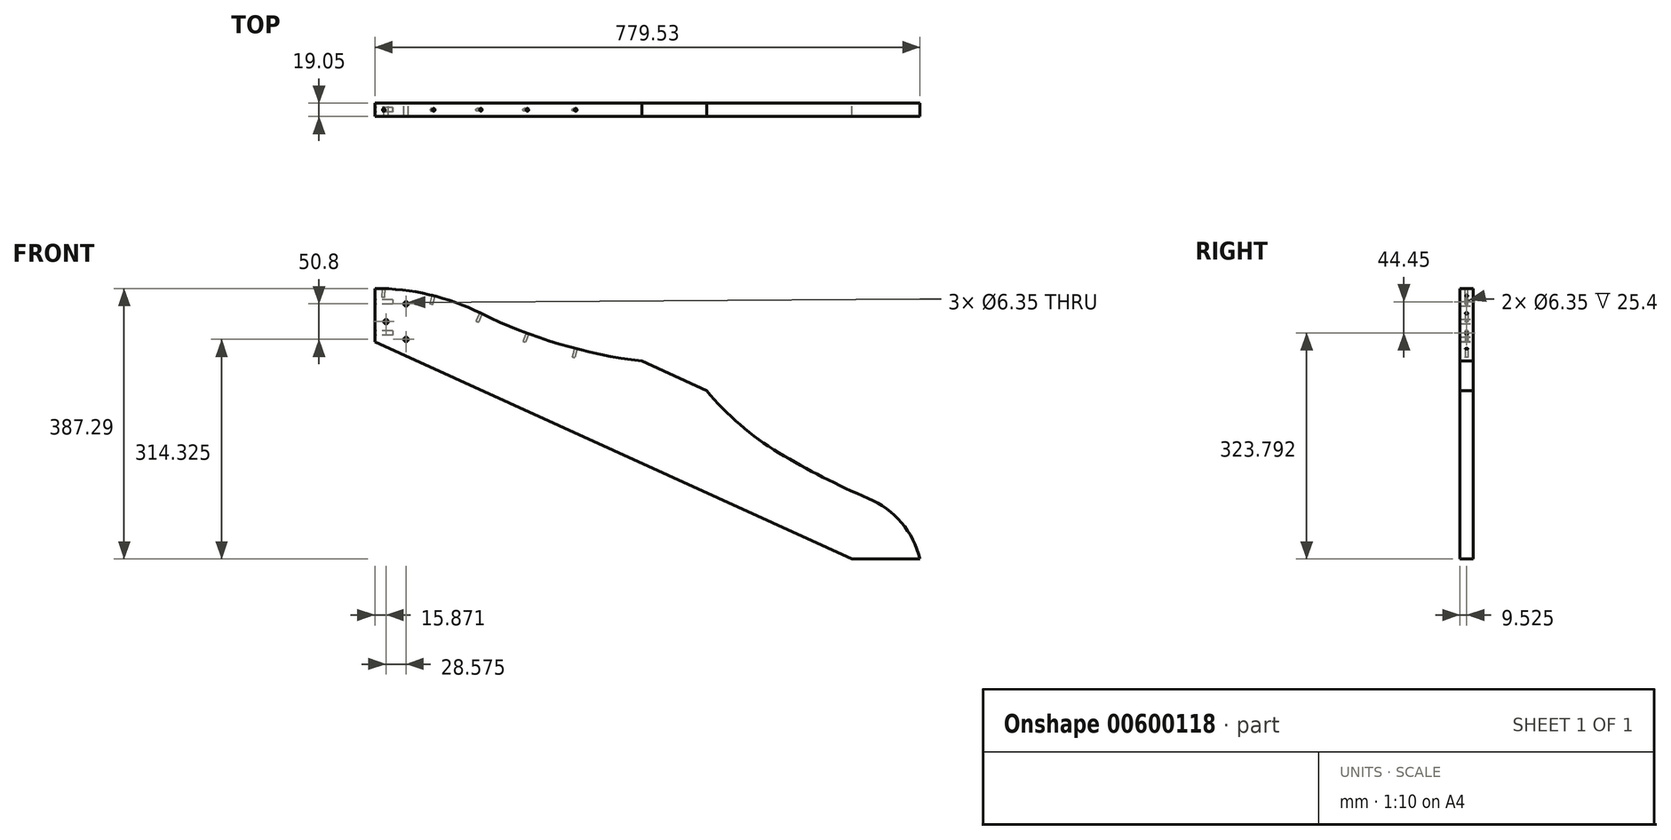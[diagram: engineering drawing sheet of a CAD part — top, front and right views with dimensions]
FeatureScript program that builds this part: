
annotation { "Feature Type Name" : "Feature", "Feature Type Description" : "" }
export const myFeature = defineFeature(function(context is Context, id is Id, definition is map)
    precondition{}
    {
        {
            var Q0;
            Q0=qCreatedBy(makeId("Front.planeOp"),FACE);
            var sketch = newSketch(context, id + "F0", { "sketchPlane" : qUnion([Q0])});
            skLineSegment(sketch, "E0", {"start": v(-749.3, 0) * mm, "end": v(-781.05, 69.67) * mm});
            skLineSegment(sketch, "E1", {"start": v(-390.53, 133.35) * mm, "end": v(-288.93, 133.35) * mm});
            skArc(sketch, "E2", {"start": v(-628.65, 100.15) * mm, "mid": v(-706.61, 93.72) * mm, "end": v(-781.05, 69.67) * mm});
            skArc(sketch, "E3", {"start": v(-628.65, 100.15) * mm, "mid": v(-508.16, 106.52) * mm, "end": v(-390.52, 133.35) * mm});
            skPoint(sketch, "E4", {"position": v(88.9, 40.51) * mm});
            skLineSegment(sketch, "E5", {"start": v(0, 0) * mm, "end": v(-749.3, 0) * mm});
            skLineSegment(sketch, "E6", {"start": v(0, 0) * mm, "end": v(88.9, 40.51) * mm});
            skArc(sketch, "E7", {"start": v(-288.93, 133.35) * mm, "mid": v(-225.13, 108.78) * mm, "end": v(-158.13, 95.25) * mm});
            skArc(sketch, "E8", {"start": v(-158.13, 95.25) * mm, "mid": v(-86.32, 89.52) * mm, "end": v(-14.28, 88.9) * mm});
            skArc(sketch, "E9", {"start": v(88.9, 40.51) * mm, "mid": v(43.04, 76.93) * mm, "end": v(-14.28, 88.9) * mm});
            skLineSegment(sketch, "E10", {"start": v(0, 0) * mm, "end": v(-620.44, -282.75) * mm, "construction": true});
            skLineSegment(sketch, "E11", {"start": v(-620.44, -282.75) * mm, "end": v(-749.3, 0) * mm, "construction": true});
            skLineSegment(sketch, "E12", {"start": v(-731.4, 67.93) * mm, "end": v(-710.34, 21.7) * mm, "construction": true});
            skLineSegment(sketch, "E13", {"start": v(-720.88, 44.82) * mm, "end": v(-746.88, 32.97) * mm, "construction": true});
            skCircle(sketch, "E14", {"center": v(-731.4, 67.93) * mm, "radius": 3.18 * mm});
            skCircle(sketch, "E15", {"center": v(-710.34, 21.7) * mm, "radius": 3.18 * mm});
            skCircle(sketch, "E16", {"center": v(-746.88, 32.97) * mm, "radius": 3.18 * mm});
            skLineSegment(sketch, "E17.bottom", {"start": v(-798.38, 61.77) * mm, "end": v(-781.05, 69.67) * mm, "construction": true});
            skLineSegment(sketch, "E17.top", {"start": v(-761.52, -19.13) * mm, "end": v(-744.18, -11.23) * mm, "construction": true});
            skLineSegment(sketch, "E17.left", {"start": v(-798.38, 61.77) * mm, "end": v(-761.52, -19.13) * mm, "construction": true});
            skLineSegment(sketch, "E17.right", {"start": v(-781.05, 69.67) * mm, "end": v(-744.18, -11.23) * mm, "construction": true});
            skLineSegment(sketch, "E18", {"start": v(0, 0) * mm, "end": v(97.7, 0) * mm, "construction": true});
            skLineSegment(sketch, "E19", {"start": v(97.7, 0) * mm, "end": v(88.9, 40.51) * mm, "construction": true});
            skLineSegment(sketch, "E20", {"start": v(-719.34, 102.7) * mm, "end": v(-674.51, 4.33) * mm, "construction": true});
            skSolve(sketch);
        }
        {
            var Q0;
            Q0=qCreatedBy(makeId("Front.planeOp"),FACE);
            var sketch = newSketch(context, id + "F1", { "sketchPlane" : qUnion([Q0])});
            skArc(sketch, "E21", {"start": v(-626.17, 175.74) * mm, "mid": v(-742.2, 163.18) * mm, "end": v(-850.18, 118.89) * mm, "construction": true});
            skArc(sketch, "E22", {"start": v(-626.17, 175.74) * mm, "mid": v(-492.66, 185.6) * mm, "end": v(-364.26, 223.48) * mm, "construction": true});
            skLineSegment(sketch, "E23", {"start": v(-605.52, 804.8) * mm, "end": v(-605.52, 101.3) * mm, "construction": true});
            skLineSegment(sketch, "E24", {"start": v(-805.94, 80.59) * mm, "end": v(-798.84, 62.9) * mm, "construction": true});
            skLineSegment(sketch, "E25", {"start": v(-798.84, 62.9) * mm, "end": v(-739.92, 86.57) * mm, "construction": true});
            skLineSegment(sketch, "E26", {"start": v(-739.92, 86.57) * mm, "end": v(-747.01, 104.25) * mm, "construction": true});
            skLineSegment(sketch, "E27", {"start": v(-747.01, 104.25) * mm, "end": v(-805.94, 80.59) * mm, "construction": true});
            skLineSegment(sketch, "E28", {"start": v(-731.46, 89.3) * mm, "end": v(-668.96, 100.57) * mm, "construction": true});
            skLineSegment(sketch, "E29", {"start": v(-668.96, 100.57) * mm, "end": v(-672.34, 119.31) * mm, "construction": true});
            skLineSegment(sketch, "E30", {"start": v(-672.34, 119.31) * mm, "end": v(-734.83, 108.05) * mm, "construction": true});
            skLineSegment(sketch, "E31", {"start": v(-734.83, 108.05) * mm, "end": v(-731.46, 89.3) * mm, "construction": true});
            skLineSegment(sketch, "E32", {"start": v(-660.1, 119.35) * mm, "end": v(-660.08, 100.3) * mm, "construction": true});
            skLineSegment(sketch, "E33", {"start": v(-660.08, 100.3) * mm, "end": v(-596.58, 100.4) * mm, "construction": true});
            skLineSegment(sketch, "E34", {"start": v(-596.58, 100.4) * mm, "end": v(-596.6, 119.45) * mm, "construction": true});
            skLineSegment(sketch, "E35", {"start": v(-596.6, 119.45) * mm, "end": v(-660.1, 119.35) * mm, "construction": true});
            skLineSegment(sketch, "E36", {"start": v(-589.04, 119) * mm, "end": v(-587.7, 100) * mm, "construction": true});
            skLineSegment(sketch, "E37", {"start": v(-587.7, 100) * mm, "end": v(-524.35, 104.46) * mm, "construction": true});
            skLineSegment(sketch, "E38", {"start": v(-524.35, 104.46) * mm, "end": v(-525.7, 123.46) * mm, "construction": true});
            skLineSegment(sketch, "E39", {"start": v(-525.7, 123.46) * mm, "end": v(-589.04, 119) * mm, "construction": true});
            skLineSegment(sketch, "E40", {"start": v(-518.8, 124.3) * mm, "end": v(-515.53, 105.54) * mm, "construction": true});
            skLineSegment(sketch, "E41", {"start": v(-515.53, 105.54) * mm, "end": v(-452.98, 116.47) * mm, "construction": true});
            skLineSegment(sketch, "E42", {"start": v(-452.98, 116.47) * mm, "end": v(-456.26, 135.24) * mm, "construction": true});
            skLineSegment(sketch, "E43", {"start": v(-456.26, 135.24) * mm, "end": v(-518.8, 124.3) * mm, "construction": true});
            skLineSegment(sketch, "E44", {"start": v(-798.84, 62.9) * mm, "end": v(-798.38, 61.77) * mm, "construction": true});
            skLineSegment(sketch, "E45", {"start": v(-739.92, 86.57) * mm, "end": v(-739.46, 85.43) * mm, "construction": true});
            skLineSegment(sketch, "E46", {"start": v(-739.92, 86.57) * mm, "end": v(-731.46, 89.3) * mm, "construction": true});
            skLineSegment(sketch, "E47", {"start": v(-668.96, 100.57) * mm, "end": v(-660.08, 100.3) * mm, "construction": true});
            skLineSegment(sketch, "E48", {"start": v(-596.58, 100.4) * mm, "end": v(-587.7, 100) * mm, "construction": true});
            skLineSegment(sketch, "E49", {"start": v(-524.35, 104.46) * mm, "end": v(-515.53, 105.54) * mm, "construction": true});
            skLineSegment(sketch, "E50", {"start": v(-668.96, 100.57) * mm, "end": v(-668.7, 99.1) * mm, "construction": true});
            skLineSegment(sketch, "E51", {"start": v(-668.7, 99.1) * mm, "end": v(-731.2, 87.85) * mm, "construction": true});
            skLineSegment(sketch, "E52", {"start": v(-731.2, 87.85) * mm, "end": v(-731.46, 89.3) * mm, "construction": true});
            skLineSegment(sketch, "E53", {"start": v(-776.48, 92.42) * mm, "end": v(-769.38, 74.74) * mm, "construction": true});
            skLineSegment(sketch, "E54", {"start": v(-769.38, 74.74) * mm, "end": v(-703.59, 113.68) * mm, "construction": true});
            skLineSegment(sketch, "E55", {"start": v(-703.59, 113.68) * mm, "end": v(-700.21, 94.94) * mm, "construction": true});
            skLineSegment(sketch, "E56", {"start": v(-700.21, 94.94) * mm, "end": v(-628.36, 119.4) * mm, "construction": true});
            skLineSegment(sketch, "E57", {"start": v(-628.36, 119.4) * mm, "end": v(-628.36, 100.35) * mm, "construction": true});
            skLineSegment(sketch, "E58", {"start": v(-628.36, 100.35) * mm, "end": v(-557.36, 121.23) * mm, "construction": true});
            skLineSegment(sketch, "E59", {"start": v(-557.36, 121.23) * mm, "end": v(-556.02, 102.23) * mm, "construction": true});
            skLineSegment(sketch, "E60", {"start": v(-556.02, 102.23) * mm, "end": v(-487.53, 129.77) * mm, "construction": true});
            skLineSegment(sketch, "E61", {"start": v(-487.53, 129.77) * mm, "end": v(-484.16, 111.02) * mm, "construction": true});
            skLineSegment(sketch, "E62", {"start": v(-596.58, 100.4) * mm, "end": v(-596.58, 99.83) * mm, "construction": true});
            skLineSegment(sketch, "E63", {"start": v(-660.08, 100.3) * mm, "end": v(-660.08, 99.73) * mm, "construction": true});
            skSolve(sketch);
        }
        {
            var Q0;
            Q0 = qSketchRegion(id + "F0", true);
            extrude(context, id + "F2", {"entities" : qUnion([Q0]), "depth" : 19.05 * mm, "offsetDistance" : 25.4 * mm});
        }
        {
            var Q0;
            Q0=sQuery(id+"F1.wireOp",EDGE,"E53");
            var Q1;
            Q1=qCreatedBy(makeId("Front.planeOp"),FACE);
            cPlane(context, id + "F3", {"entities" : qUnion([Q0, Q1]), "cplaneType" : CPlaneType.LINE_ANGLE, "offset" : 25.4 * mm, "angle" : 90 * degree, "width" : 152.4 * mm, "height" : 152.4 * mm});
        }
        {
            var Q0;
            Q0=sQuery(id+"F1.wireOp",EDGE,"E55");
            cPlane(context, id + "F4", {"entities" : qUnion([Q0]), "cplaneType" : CPlaneType.LINE_ANGLE, "offset" : 25.4 * mm, "angle" : 0 * degree, "width" : 152.4 * mm, "height" : 152.4 * mm});
        }
        {
            var Q0;
            Q0=sQuery(id+"F1.wireOp",EDGE,"E57");
            cPlane(context, id + "F5", {"entities" : qUnion([Q0]), "cplaneType" : CPlaneType.LINE_ANGLE, "offset" : 25.4 * mm, "angle" : 0 * degree, "width" : 152.4 * mm, "height" : 152.4 * mm});
        }
        {
            var Q0;
            Q0=sQuery(id+"F1.wireOp",EDGE,"E59");
            cPlane(context, id + "F6", {"entities" : qUnion([Q0]), "cplaneType" : CPlaneType.LINE_ANGLE, "offset" : 25.4 * mm, "angle" : 0 * degree, "width" : 152.4 * mm, "height" : 152.4 * mm});
        }
        {
            var Q0;
            Q0=sQuery(id+"F1.wireOp",EDGE,"E61");
            cPlane(context, id + "F7", {"entities" : qUnion([Q0]), "cplaneType" : CPlaneType.LINE_ANGLE, "offset" : 25.4 * mm, "angle" : 0 * degree, "width" : 152.4 * mm, "height" : 152.4 * mm});
        }
        {
            var Q0;
            Q0=qCreatedBy(id+"F3.planeOp",FACE);
            var sketch = newSketch(context, id + "F8", { "sketchPlane" : qUnion([Q0])});
            skLineSegment(sketch, "E64", {"start": v(-19.05, 356.06) * mm, "end": v(0, 356.06) * mm, "construction": true});
            skLineSegment(sketch, "E65.0", {"start": v(-19.05, 327.2) * mm, "end": v(-19.05, 356.06) * mm, "construction": true});
            skLineSegment(sketch, "E66.0", {"start": v(0, 327.2) * mm, "end": v(0, 356.06) * mm, "construction": true});
            skLineSegment(sketch, "E67", {"start": v(-9.52, 355.3) * mm, "end": v(-9.52, 356.06) * mm, "construction": true});
            skLineSegment(sketch, "E68.bottom", {"start": v(-9.52, 356.06) * mm, "end": v(-7.62, 356.06) * mm});
            skLineSegment(sketch, "E68.top", {"start": v(-9.52, 343.36) * mm, "end": v(-7.62, 343.36) * mm});
            skLineSegment(sketch, "E68.left", {"start": v(-9.52, 356.06) * mm, "end": v(-9.52, 343.36) * mm});
            skLineSegment(sketch, "E68.right", {"start": v(-7.62, 356.06) * mm, "end": v(-7.62, 343.36) * mm});
            skSolve(sketch);
        }
        {
            var Q0;
            Q0 = qSketchRegion(id + "F8", true);
            var Q1;
            Q1=sQuery(id+"F8.wireOp",EDGE,"E67");
            revolve(context, id + "F9", {"operationType" : NewBodyOperationType.REMOVE, "entities" : qUnion([Q0]), "axis" : qUnion([Q1]), "revolveType" : RevolveType.FULL, "oppositeDirection" : true});
        }
        {
            var Q0;
            Q0=qCreatedBy(id+"F4.planeOp",FACE);
            var sketch = newSketch(context, id + "F10", { "sketchPlane" : qUnion([Q0])});
            skLineSegment(sketch, "E69", {"start": v(0, 217.6) * mm, "end": v(19.05, 217.6) * mm, "construction": true});
            skLineSegment(sketch, "E70.0", {"start": v(19.05, 217.6) * mm, "end": v(19.05, 207.06) * mm, "construction": true});
            skLineSegment(sketch, "E71.0", {"start": v(0, 217.6) * mm, "end": v(0, 207.06) * mm, "construction": true});
            skLineSegment(sketch, "E72", {"start": v(9.53, 204.7) * mm, "end": v(9.53, 217.6) * mm, "construction": true});
            skLineSegment(sketch, "E73.bottom", {"start": v(9.53, 217.6) * mm, "end": v(7.62, 217.6) * mm});
            skLineSegment(sketch, "E73.top", {"start": v(9.53, 204.9) * mm, "end": v(7.62, 204.9) * mm});
            skLineSegment(sketch, "E73.left", {"start": v(9.53, 217.6) * mm, "end": v(9.53, 204.9) * mm});
            skLineSegment(sketch, "E73.right", {"start": v(7.62, 217.6) * mm, "end": v(7.62, 204.9) * mm});
            skSolve(sketch);
        }
        {
            var Q0;
            Q0 = qSketchRegion(id + "F10", true);
            var Q1;
            Q1=sQuery(id+"F10.wireOp",EDGE,"E72");
            revolve(context, id + "F11", {"operationType" : NewBodyOperationType.REMOVE, "entities" : qUnion([Q0]), "axis" : qUnion([Q1]), "revolveType" : RevolveType.FULL, "oppositeDirection" : true});
        }
        {
            var Q0;
            Q0=qCreatedBy(id+"F5.planeOp",FACE);
            var sketch = newSketch(context, id + "F12", { "sketchPlane" : qUnion([Q0])});
            skLineSegment(sketch, "E74.0", {"start": v(0, 99.77) * mm, "end": v(0, 133.35) * mm, "construction": true});
            skLineSegment(sketch, "E75.0", {"start": v(19.05, 99.77) * mm, "end": v(19.05, 133.35) * mm, "construction": true});
            skLineSegment(sketch, "E76", {"start": v(19.05, 99.77) * mm, "end": v(0, 99.77) * mm, "construction": true});
            skLineSegment(sketch, "E77", {"start": v(9.52, 99.77) * mm, "end": v(9.53, 78.2) * mm, "construction": true});
            skLineSegment(sketch, "E78.bottom", {"start": v(9.52, 99.77) * mm, "end": v(11.43, 99.77) * mm, "construction": true});
            skLineSegment(sketch, "E78.top", {"start": v(9.53, 87.07) * mm, "end": v(11.43, 87.07) * mm});
            skLineSegment(sketch, "E78.left", {"start": v(9.52, 99.77) * mm, "end": v(9.52, 87.07) * mm});
            skLineSegment(sketch, "E78.right", {"start": v(11.43, 99.77) * mm, "end": v(11.43, 87.07) * mm});
            skLineSegment(sketch, "E79", {"start": v(9.52, 99.77) * mm, "end": v(9.52, 104) * mm});
            skLineSegment(sketch, "E80", {"start": v(9.53, 104) * mm, "end": v(11.43, 104) * mm});
            skLineSegment(sketch, "E81", {"start": v(11.43, 104) * mm, "end": v(11.43, 99.77) * mm});
            skSolve(sketch);
        }
        {
            var Q0;
            Q0 = qSketchRegion(id + "F12", true);
            var Q1;
            Q1=sQuery(id+"F12.wireOp",EDGE,"E77");
            revolve(context, id + "F13", {"operationType" : NewBodyOperationType.REMOVE, "entities" : qUnion([Q0]), "axis" : qUnion([Q1]), "revolveType" : RevolveType.FULL, "oppositeDirection" : true});
        }
        {
            var Q0;
            Q0=qCreatedBy(id+"F6.planeOp",FACE);
            var sketch = newSketch(context, id + "F14", { "sketchPlane" : qUnion([Q0])});
            skLineSegment(sketch, "E82.0", {"start": v(0, 140.33) * mm, "end": v(0, 160.46) * mm, "construction": true});
            skLineSegment(sketch, "E83.0", {"start": v(19.05, 140.33) * mm, "end": v(19.05, 160.46) * mm, "construction": true});
            skLineSegment(sketch, "E84", {"start": v(19.05, 140.33) * mm, "end": v(0, 140.33) * mm, "construction": true});
            skLineSegment(sketch, "E85", {"start": v(9.53, 140.33) * mm, "end": v(9.53, 115.39) * mm, "construction": true});
            skPoint(sketch, "E85.endSnap0", {"position": v(9.53, 140.33) * mm});
            skLineSegment(sketch, "E86.bottom", {"start": v(9.53, 140.33) * mm, "end": v(11.43, 140.33) * mm});
            skLineSegment(sketch, "E86.top", {"start": v(9.53, 127.63) * mm, "end": v(11.43, 127.63) * mm});
            skLineSegment(sketch, "E86.left", {"start": v(9.53, 140.33) * mm, "end": v(9.53, 127.63) * mm});
            skLineSegment(sketch, "E86.right", {"start": v(11.43, 140.33) * mm, "end": v(11.43, 127.63) * mm});
            skSolve(sketch);
        }
        {
            var Q0;
            Q0 = qSketchRegion(id + "F14", true);
            var Q1;
            Q1=sQuery(id+"F14.wireOp",EDGE,"E85");
            revolve(context, id + "F15", {"operationType" : NewBodyOperationType.REMOVE, "entities" : qUnion([Q0]), "axis" : qUnion([Q1]), "revolveType" : RevolveType.FULL, "oppositeDirection" : true});
        }
        {
            var Q0;
            Q0=qCreatedBy(id+"F7.planeOp",FACE);
            var sketch = newSketch(context, id + "F16", { "sketchPlane" : qUnion([Q0])});
            skLineSegment(sketch, "E87.0", {"start": v(0, 210.03) * mm, "end": v(0, 194.39) * mm, "construction": true});
            skLineSegment(sketch, "E88.0", {"start": v(19.05, 210.03) * mm, "end": v(19.05, 194.39) * mm, "construction": true});
            skLineSegment(sketch, "E89.bottom", {"start": v(9.53, 194.39) * mm, "end": v(11.43, 194.39) * mm, "construction": true});
            skLineSegment(sketch, "E89.top", {"start": v(9.53, 181.69) * mm, "end": v(11.43, 181.69) * mm});
            skLineSegment(sketch, "E89.left", {"start": v(11.43, 194.39) * mm, "end": v(11.43, 181.69) * mm});
            skLineSegment(sketch, "E89.right", {"start": v(9.53, 194.39) * mm, "end": v(9.53, 181.69) * mm});
            skLineSegment(sketch, "E90", {"start": v(9.53, 194.39) * mm, "end": v(9.53, 174.69) * mm, "construction": true});
            skLineSegment(sketch, "E91", {"start": v(9.53, 194.39) * mm, "end": v(9.53, 203.86) * mm});
            skLineSegment(sketch, "E92", {"start": v(9.53, 203.86) * mm, "end": v(11.43, 203.86) * mm});
            skLineSegment(sketch, "E93", {"start": v(11.43, 203.86) * mm, "end": v(11.43, 194.39) * mm});
            skLineSegment(sketch, "E94", {"start": v(19.05, 194.39) * mm, "end": v(0, 194.39) * mm, "construction": true});
            skSolve(sketch);
        }
        {
            var Q0;
            Q0 = qSketchRegion(id + "F16", true);
            var Q1;
            Q1=sQuery(id+"F16.wireOp",EDGE,"E90");
            revolve(context, id + "F17", {"operationType" : NewBodyOperationType.REMOVE, "entities" : qUnion([Q0]), "axis" : qUnion([Q1]), "revolveType" : RevolveType.FULL, "oppositeDirection" : true});
        }
        {
            var Q0;
            Q0=makeQuery(id+"F2.opExtrude","SWEPT_FACE",FACE,{"disambiguationData":[OSD([sQuery(id+"F0.wireOp",EDGE,"E0")])]});
            var sketch = newSketch(context, id + "F18", { "sketchPlane" : qUnion([Q0])});
            skLineSegment(sketch, "E95.0.0", {"start": v(0, 387.3) * mm, "end": v(0, 310.73) * mm, "construction": true});
            skLineSegment(sketch, "E95.0.1", {"start": v(0, 310.73) * mm, "end": v(19.05, 310.73) * mm, "construction": true});
            skLineSegment(sketch, "E95.0.2", {"start": v(19.05, 310.73) * mm, "end": v(19.05, 387.3) * mm, "construction": true});
            skLineSegment(sketch, "E95.0.3", {"start": v(19.05, 387.3) * mm, "end": v(0, 387.3) * mm, "construction": true});
            skLineSegment(sketch, "E96", {"start": v(9.53, 387.3) * mm, "end": v(9.53, 368.24) * mm, "construction": true});
            skLineSegment(sketch, "E97", {"start": v(9.53, 368.24) * mm, "end": v(9.53, 323.8) * mm, "construction": true});
            skCircle(sketch, "E98", {"center": v(9.53, 368.24) * mm, "radius": 3.18 * mm});
            skCircle(sketch, "E99", {"center": v(9.53, 323.8) * mm, "radius": 3.18 * mm});
            skSolve(sketch);
        }
        {
            var Q0;
            Q0 = qSketchRegion(id + "F18", true);
            extrude(context, id + "F19", {"entities" : qUnion([Q0]), "operationType" : NewBodyOperationType.REMOVE, "oppositeDirection" : true, "depth" : 25.4 * mm, "offsetDistance" : 25.4 * mm});
        }
        {
            var Q0;
            Q0=makeQuery(id+"F2.opExtrude","SWEPT_BODY",BODY,{"disambiguationData":[OSD([sQuery(id+"F0.wireOp",EDGE,"E0"),sQuery(id+"F0.wireOp",EDGE,"E1"),sQuery(id+"F0.wireOp",EDGE,"E2"),sQuery(id+"F0.wireOp",EDGE,"E3"),sQuery(id+"F0.wireOp",EDGE,"E5"),sQuery(id+"F0.wireOp",EDGE,"E6"),sQuery(id+"F0.wireOp",EDGE,"E7"),sQuery(id+"F0.wireOp",EDGE,"E8"),sQuery(id+"F0.wireOp",EDGE,"E9"),sQuery(id+"F0.wireOp",EDGE,"E14"),sQuery(id+"F0.wireOp",EDGE,"E15"),sQuery(id+"F0.wireOp",EDGE,"E16")])]});
            var Q1;
            Q1=makeQuery(id+"F2.opExtrude","SWEPT_EDGE",EDGE,{"disambiguationData":[OSD([sQuery(id+"F0.wireOp",EDGE,"E5"),sQuery(id+"F0.wireOp",EDGE,"E6")])]});
            transform(context, id + "F20", {"entities" : qUnion([Q0]), "transformType" : TransformType.ROTATION, "transformAxis" : qUnion([Q1]), "angle" : 24.5 * degree, "makeCopy" : false});
        }
    });
